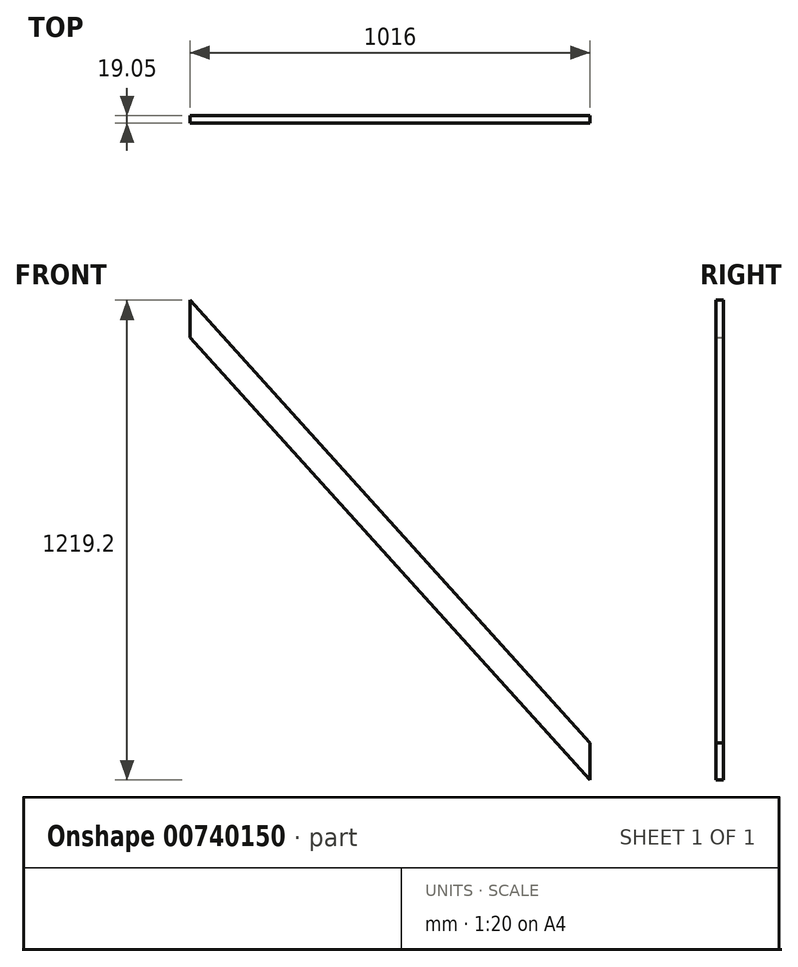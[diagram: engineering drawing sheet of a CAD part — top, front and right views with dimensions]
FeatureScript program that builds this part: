
annotation { "Feature Type Name" : "Feature", "Feature Type Description" : "" }
export const myFeature = defineFeature(function(context is Context, id is Id, definition is map)
    precondition{}
    {
        {
            var Q0;
            Q0=qCreatedBy(makeId("Front.planeOp"),FACE);
            var sketch = newSketch(context, id + "F0", { "sketchPlane" : qUnion([Q0])});
            skLineSegment(sketch, "E0.bottom", {"start": v(-310.98, 567.05) * mm, "end": v(705.02, 567.05) * mm});
            skLineSegment(sketch, "E0.top", {"start": v(-310.98, -652.15) * mm, "end": v(705.02, -652.15) * mm});
            skLineSegment(sketch, "E0.left", {"start": v(-310.98, 567.05) * mm, "end": v(-310.98, -652.15) * mm});
            skLineSegment(sketch, "E0.right", {"start": v(705.02, 567.05) * mm, "end": v(705.02, -652.15) * mm});
            skLineSegment(sketch, "E1.bottom", {"start": v(-310.98, 567.05) * mm, "end": v(752.14, -609.58) * mm});
            skLineSegment(sketch, "E1.top", {"start": v(-358.1, 524.48) * mm, "end": v(705.02, -652.15) * mm});
            skLineSegment(sketch, "E1.left", {"start": v(-310.98, 567.05) * mm, "end": v(-358.1, 524.48) * mm});
            skLineSegment(sketch, "E1.right", {"start": v(752.14, -609.58) * mm, "end": v(705.02, -652.15) * mm});
            skPoint(sketch, "E1.middle", {"position": v(197.02, -42.55) * mm});
            skPoint(sketch, "E1.middle.positionSnap0", {"position": v(197.02, 567.05) * mm});
            skPoint(sketch, "E1.middle.positionSnap1", {"position": v(-310.98, -42.55) * mm});
            skPoint(sketch, "E1.centerSnap0", {"position": v(197.02, 567.05) * mm});
            skPoint(sketch, "E1.centerSnap1", {"position": v(-310.98, -42.55) * mm});
            skSolve(sketch);
        }
        {
            var Q0;
            {var subQ1=sQuery(id+"F0.wireOp",EDGE,"E0.left");var subQ3=sQuery(id+"F0.wireOp",EDGE,"E1.top");var subQ4=makeQuery(id+"F0.imprint","INTERSECT",VERTEX,{"derivedFrom":[subQ1,subQ3]});Q0=makeQuery(id+"F0.imprint","IMPRINT",FACE,{"disambiguationData":[TD([[makeQuery(id+"F0.imprint","IMPRINT",EDGE,{"disambiguationData":[TD([[subQ4,1.0]])],"derivedFrom":subQ1}),1.0]])]});}
            extrude(context, id + "F1", {"entities" : qUnion([Q0]), "depth" : 19.05 * mm, "offsetDistance" : 25.4 * mm});
        }
    });
